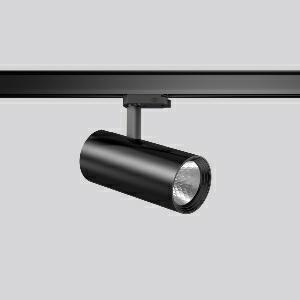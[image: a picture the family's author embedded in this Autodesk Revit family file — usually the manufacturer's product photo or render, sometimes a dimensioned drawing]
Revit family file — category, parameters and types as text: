
# Revit family: deecos_s_mini_742197_003_1_e657
name_source: partatom
category: Lighting Fixtures
units: mm (PartAtom-declared; Revit-internal decimal feet)

## family parameters
Cut with Voids When Loaded = No
Host = Face
Light Source = No
Part Type = Normal
Room Calculation Point = No
Round Connector Dimension = Use Diameter
Shared = No

## types (1)
- DEECOS S mini (1 x LED Modul 940, 2750 lm, 4000)
    Apparent Load = 20 VA
    Approval mark = CE
    CIE Flux Codes = 95 99 100 100 100
    Color Rendering = 92
    Color Temperature = 4000
    Default Elevation = 1800 mm
    Description = Series: DEECOS S mini
LED surface-mounted projector in modern design with no visible cooling ribs. Housing: die-cast aluminium, powder-coated. Rotation range: 356°. Swivel range: 90°. Black plastic ring and recessed LED to prevent glare from the side. Optical assembly with reflector made of MIRO-Silver with 98% total light reflection for outstanding efficiency - can be changed without tools. Best colour rendering index Ra>90. With multi adaptor for 3-circuit tracks 230 V. Suitable for Track on ceiling, Wall track. High quality converter without flickering and stroboscopic effect. The following accessories can be mounted without use of tools: interchangeable lenses, decorative glasses, honeycomb louvre, clear and frosted diffusers, white interchangeable plastic ring. 
Colour: deep black, matt (RAL 9005)
Diameter: 87 mm
Height: 214 mm
Lamp: LED
Socket: without socket
Colour temperature: 4000K
Colour rendering index (CRI): 92
System power: 20 W
Rated luminous flux: 2750 lm
Luminous efficiency: 138 lm/W
Control gear: Regulated power supply
Protection class: I
Type of protection: IP 20
    Height = 214 mm
    Lamp = 1 x LED Modul 940
    Lamp Light Flux = 2750 lm
    Lamp count = 1
    Length = 87 mm
    Lifetime = 50000 h
    Luminous efficacy = 138 lm/W
    Manufacturer = RZB
    ModVariant = No
    Model = 742197.003.1
    Mounting Place = Ceiling
    Mounting Type = Rail mounted
    Number of Poles = 1
    OnlyDefault = Yes
    Power Factor = 1
    Product Name = DEECOS S mini
    Product group = Track mounted projectors
    ProductGroupID = 301
    Protection Class = Protection class I
    Protection Degree = IP 20
    RLX_Detail_Level = 1
    RLX_Emergency_Light_Flux = 0 lm
    RLX_Emergency_Type = 0
    RLX_Emergency_Type_DB = No
    RlxData = <blob elided: 38841 chars, md5=01a4ecf6>
    Socket = socket
    Standby Power = 0 W
    System Light Flux = 2750 lm
    System Power = 20 W
    Type Comments = Product without accessories
    Type Image = 741926.003.jpg
    URL = http://relux.com
    VarID = ---
    Voltage = 230 V
    Voltage Range = 220-240 V
    Weight = 0.00 kg
    Width = 0 mm  [stored 0 ft]

note: [stored X ft] marks values corroborated as IEEE doubles in the binary element streams (Revit-internal decimal feet)

## geometry (parser evidence)
native form markers: Blend x4, Sweep x12
no freeform markers — native parametric forms only
